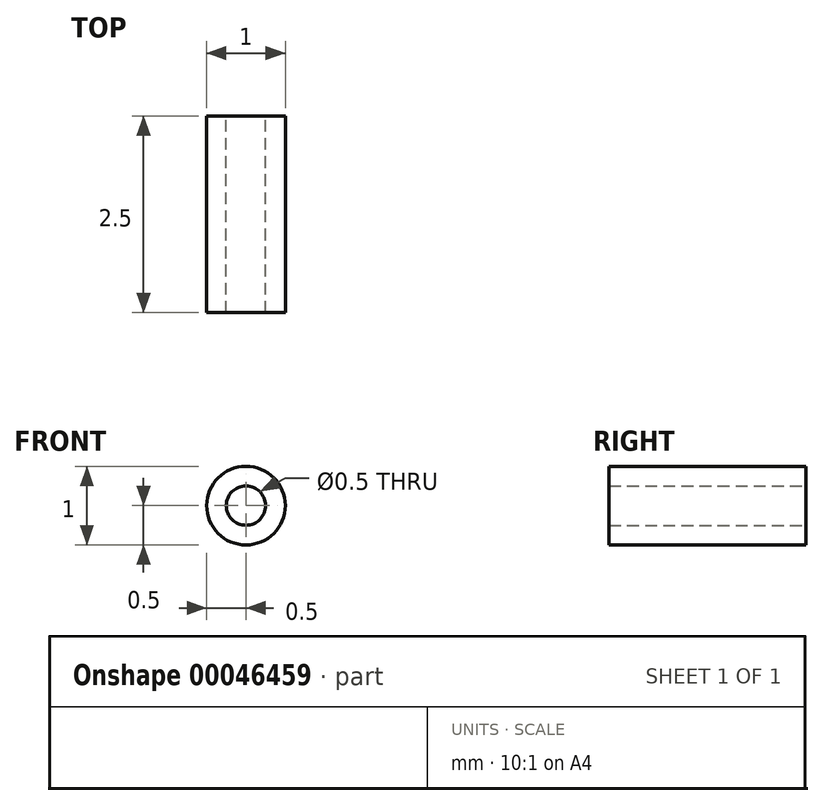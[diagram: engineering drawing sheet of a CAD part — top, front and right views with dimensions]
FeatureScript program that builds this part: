
annotation { "Feature Type Name" : "Feature", "Feature Type Description" : "" }
export const myFeature = defineFeature(function(context is Context, id is Id, definition is map)
    precondition{}
    {
        {
            var Q0;
            Q0=qCreatedBy(makeId("Front.planeOp"),FACE);
            var sketch = newSketch(context, id + "F0", { "sketchPlane" : qUnion([Q0])});
            skCircle(sketch, "E0", {"center": v(0, 0) * mm, "radius": 0.5 * mm});
            skCircle(sketch, "E1", {"center": v(0, 0) * mm, "radius": 0.25 * mm});
            skSolve(sketch);
        }
        {
            var Q0;
            Q0=makeQuery(id+"F0.imprint","IMPRINT",FACE,{"disambiguationData":[TD([[makeQuery(id+"F0.imprint","IMPRINT",EDGE,{"derivedFrom":sQuery(id+"F0.wireOp",EDGE,"E0")}),1.0]])]});
            extrude(context, id + "F1", {"entities" : qUnion([Q0]), "depth" : 2.5 * mm});
        }
    });
